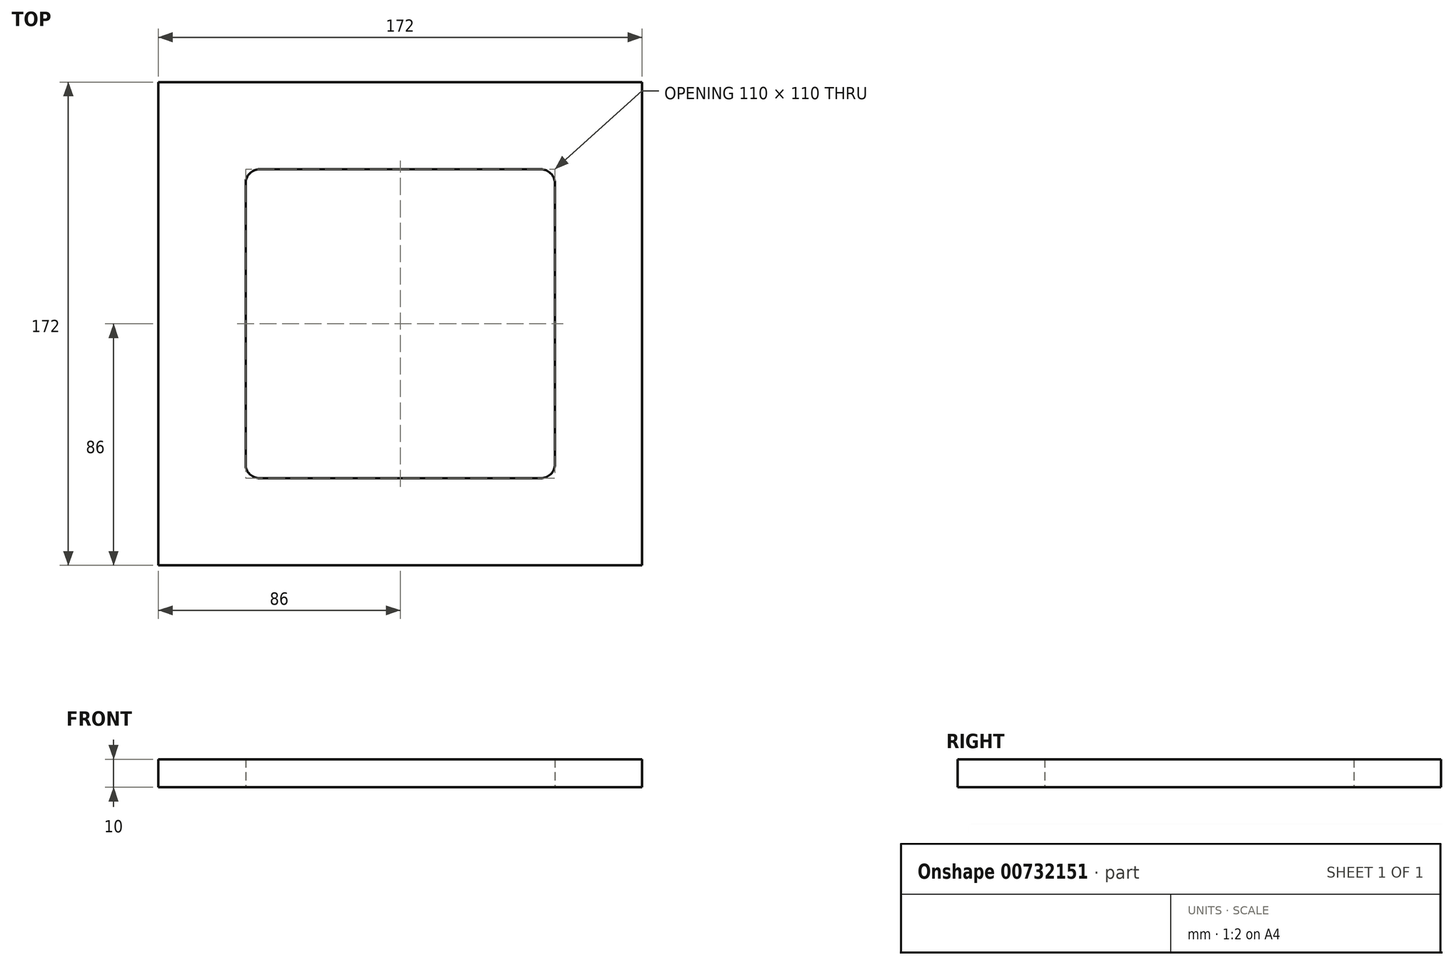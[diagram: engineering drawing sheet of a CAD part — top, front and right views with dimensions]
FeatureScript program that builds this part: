
annotation { "Feature Type Name" : "Feature", "Feature Type Description" : "" }
export const myFeature = defineFeature(function(context is Context, id is Id, definition is map)
    precondition{}
    {
        {
            var Q0;
            Q0=qCreatedBy(makeId("Top.planeOp"),FACE);
            var sketch = newSketch(context, id + "F0", { "sketchPlane" : qUnion([Q0])});
            skLineSegment(sketch, "E0.bottom", {"start": v(-86, 86) * mm, "end": v(86, 86) * mm});
            skLineSegment(sketch, "E0.top", {"start": v(-86, -86) * mm, "end": v(86, -86) * mm});
            skLineSegment(sketch, "E0.left", {"start": v(-86, 86) * mm, "end": v(-86, -86) * mm});
            skLineSegment(sketch, "E0.right", {"start": v(86, 86) * mm, "end": v(86, -86) * mm});
            skPoint(sketch, "E0.middle", {"position": v(0, 0) * mm});
            skSolve(sketch);
        }
        {
            var Q0;
            Q0=qSketchRegion(id+"F0",true);
            extrude(context, id + "F1", {"entities" : qUnion([Q0]), "depth" : 10 * mm, "offsetDistance" : 25 * mm});
        }
        {
            var Q0;
            Q0=qCreatedBy(makeId("Top.planeOp"),FACE);
            var sketch = newSketch(context, id + "F2", { "sketchPlane" : qUnion([Q0])});
            skLineSegment(sketch, "E1.bottom", {"start": v(-55, 55) * mm, "end": v(55, 55) * mm});
            skLineSegment(sketch, "E1.top", {"start": v(-55, -55) * mm, "end": v(55, -55) * mm});
            skLineSegment(sketch, "E1.left", {"start": v(-55, 55) * mm, "end": v(-55, -55) * mm});
            skLineSegment(sketch, "E1.right", {"start": v(55, 55) * mm, "end": v(55, -55) * mm});
            skPoint(sketch, "E1.middle", {"position": v(0, 0) * mm});
            skSolve(sketch);
        }
        {
            var Q0;
            Q0=qSketchRegion(id+"F2",true);
            extrude(context, id + "F3", {"entities" : qUnion([Q0]), "operationType" : NewBodyOperationType.REMOVE, "depth" : 45 * mm, "offsetDistance" : 25 * mm});
        }
        {
            var Q0;
            Q0=makeQuery(id+"F3.boolean.opBoolean","COPY",EDGE,{"derivedFrom":makeQuery(id+"F3.opExtrude","SWEPT_EDGE",EDGE,{"disambiguationData":[OSD([sQuery(id+"F2.wireOp",EDGE,"E1.bottom"),sQuery(id+"F2.wireOp",EDGE,"E1.right")])]})});
            var Q1;
            Q1=makeQuery(id+"F3.boolean.opBoolean","COPY",EDGE,{"derivedFrom":makeQuery(id+"F3.opExtrude","SWEPT_EDGE",EDGE,{"disambiguationData":[OSD([sQuery(id+"F2.wireOp",EDGE,"E1.top"),sQuery(id+"F2.wireOp",EDGE,"E1.right")])]})});
            var Q2;
            Q2=makeQuery(id+"F3.boolean.opBoolean","COPY",EDGE,{"derivedFrom":makeQuery(id+"F3.opExtrude","SWEPT_EDGE",EDGE,{"disambiguationData":[OSD([sQuery(id+"F2.wireOp",EDGE,"E1.top"),sQuery(id+"F2.wireOp",EDGE,"E1.left")])]})});
            var Q3;
            Q3=makeQuery(id+"F3.boolean.opBoolean","COPY",EDGE,{"derivedFrom":makeQuery(id+"F3.opExtrude","SWEPT_EDGE",EDGE,{"disambiguationData":[OSD([sQuery(id+"F2.wireOp",EDGE,"E1.bottom"),sQuery(id+"F2.wireOp",EDGE,"E1.left")])]})});
            fillet(context, id + "F4", {"entities" : qUnion([Q0, Q1, Q2, Q3]), "radius" : 5 * mm, "tangentPropagation" : true, "allowEdgeOverflow" : false});
        }
    });
